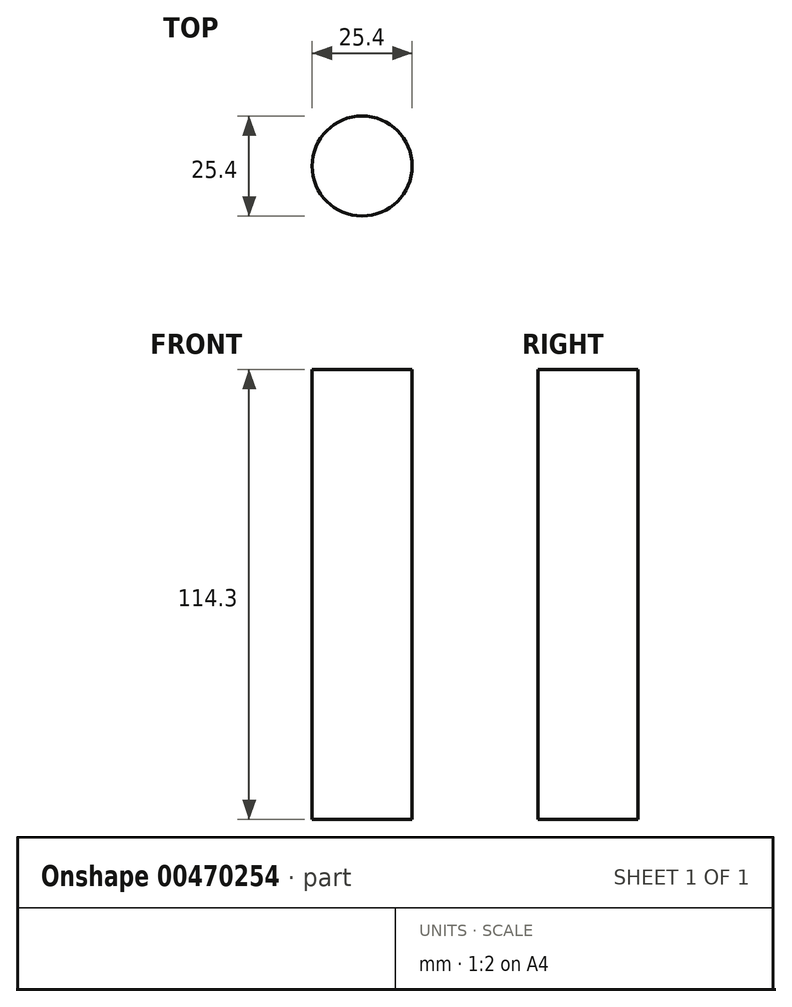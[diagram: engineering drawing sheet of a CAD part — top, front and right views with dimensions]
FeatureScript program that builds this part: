
annotation { "Feature Type Name" : "Feature", "Feature Type Description" : "" }
export const myFeature = defineFeature(function(context is Context, id is Id, definition is map)
    precondition{}
    {
        {
            var Q0;
            Q0=qCreatedBy(makeId("Top.planeOp"),FACE);
            var sketch = newSketch(context, id + "F0", { "sketchPlane" : qUnion([Q0])});
            skCircle(sketch, "E0", {"center": v(0, 0) * mm, "radius": 12.7 * mm});
            skSolve(sketch);
        }
        {
            var Q0;
            Q0=makeQuery(id+"F0.imprint","IMPRINT",FACE,{"disambiguationData":[TD([[makeQuery(id+"F0.imprint","IMPRINT",EDGE,{"derivedFrom":sQuery(id+"F0.wireOp",EDGE,"E0")}),1.0]])]});
            extrude(context, id + "F1", {"entities" : qUnion([Q0]), "endBound" : BoundingType.SYMMETRIC, "depth" : 114.3 * mm});
        }
    });
